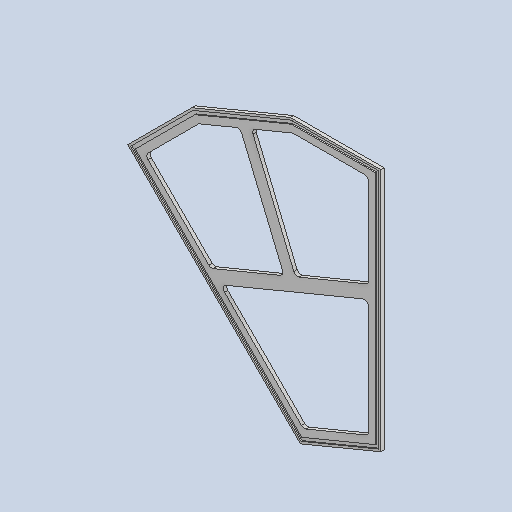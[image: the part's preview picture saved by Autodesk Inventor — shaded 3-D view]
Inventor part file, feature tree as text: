
AUTODESK INVENTOR PART (.ipt)
format: ipt  version: 2025 (Build 290162010, 162A)  size: 188,416 bytes
history: native  units: mm
features: extrude x3, fillet x3, sketch x3
ambient origin geometry x8: Origin, YZ Plane, XZ Plane, XY Plane, X Axis, Y Axis, Z Axis, Center Point
bodies: Solid1 (feature_tree)
feature tree (9):
  extrude  "Extrusion1"  Depth=260.0mm
  extrude  "Extrusion2"  Depth=8.0mm TaperAngle=0.0deg
  fillet  "Fillet1"  Radius=15.0mm
  extrude  "Extrusion3"  Depth=280.0mm
  fillet  "Fillet3"  Radius=30.0mm
  fillet  "Fillet4"  Radius=30.0mm
  sketch  "Sketch1"  dims[d0=513.0mm d2=260.0mm]
  sketch  "Sketch2"  dims[d3=635.0mm d5=8.0mm d6=0.0mm d10=15.0mm]
  sketch  "Sketch4"  dims[d11=30.0mm d12=280.0mm d13=30.0mm d14=30.0mm d15=15.0mm d16=0.0mm d17=0.0mm d18=10.0mm d21=30.0mm d22=30.0mm d23=30.0mm d24=30.0mm d26=5.0mm d27=8.0mm d28=3.0mm d29=0.0mm d30=16.0mm d31=8.0mm]
